# Revit family: Toilet_Seat-Elongated_Closed_Front-KOHLER-Bancroft-K-4685
name_source: partatom
category: Specialty Equipment
revit_build: Autodesk Revit 2015 (Build: 20140606_1530(x64)
units: mm (PartAtom-declared; Revit-internal decimal feet)

## types (6) — shared parameters
ADA Compliant = No
Assembly Code = C1030200
Date Modified = 12/24/2018
Default Elevation = 0"
Height = 1"
Length = 17 13/16"
Manufacturer = KOHLER Co.
MasterFormat 1995 = 10820
MasterFormat 2004 = 10.28.13
Material = Plastic
Product Documentation Link = http://www.us.kohler.com
Product Name = Bancroft
Product Page URL = http://www.us.kohler.com
URL = https://www.us.kohler.com
Width = 14 3/16"

## per-type parameters (varying)
| type | Description | Finish | Hinge Material | Model | Type |
| Polished Chrome Hinges, 0-White | Elongated toilet seat with Polished Chrome hinges | Kohler-Plastic-0-White | Kohler-Metal-CP-Polished_Chrome | K-4685-CP-0 | 1 |
| Polished Chrome Hinges, 96-Biscuit | Elongated toilet seat with Polished Chrome hinges | Kohler-Plastic-96-Biscuit | Kohler-Metal-CP-Polished_Chrome | K-4685-CP-96 | 2 |
| Polished Chrome Hinges, 47-Almond | Elongated toilet seat with Polished Chrome hinges | Kohler-Plastic-47-Almond | Kohler-Metal-CP-Polished_Chrome | K-4685-CP-47 | 3 |
| Brushed Nicke Hinges, 47-Almond | Elongated toilet seat with Vibrant Brushed Nickel hinges | Kohler-Plastic-47-Almond | Kohler-Metal-BN-Vibrant_Brushed_Nickel | K-4685-BN-47 | 6 |
| Brushed Nickel Hinges, 0-White | Elongated toilet seat with Vibrant Brushed Nickel hinges | Kohler-Plastic-0-White | Kohler-Metal-BN-Vibrant_Brushed_Nickel | K-4685-BN-0 | 4 |
| Brushed Nicke Hinges, 96-Biscuit | Elongated toilet seat with Vibrant Brushed Nickel hinges | Kohler-Plastic-96-Biscuit | Kohler-Metal-BN-Vibrant_Brushed_Nickel | K-4685-BN-96 | 5 |

## geometry (parser evidence)
native form markers: Sweep x5
no freeform markers — native parametric forms only
